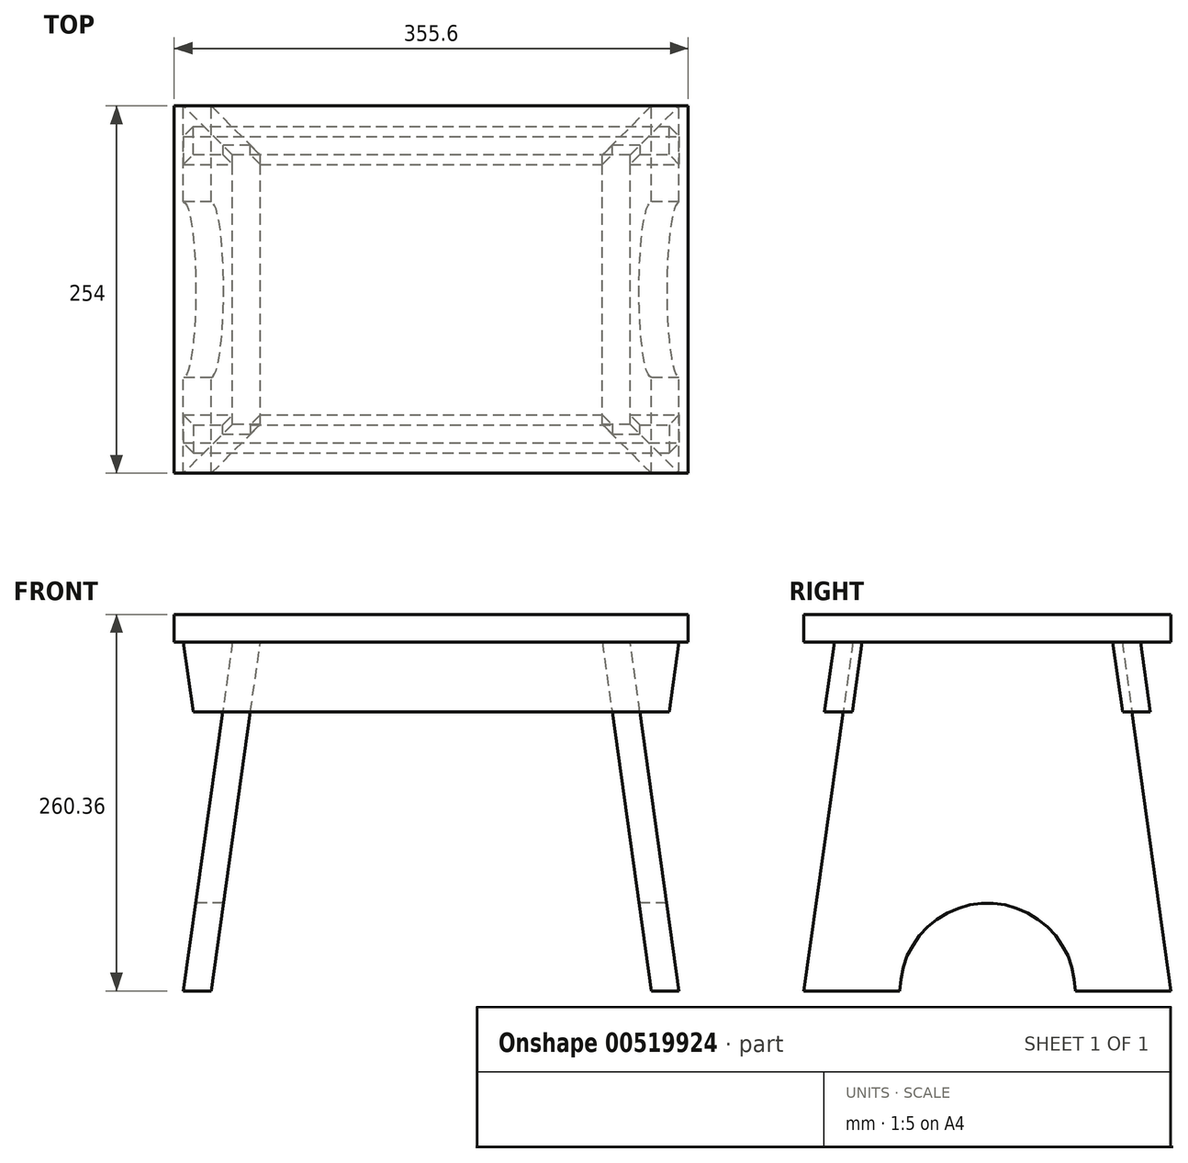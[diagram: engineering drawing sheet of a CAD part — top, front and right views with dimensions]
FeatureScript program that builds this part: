
annotation { "Feature Type Name" : "Feature", "Feature Type Description" : "" }
export const myFeature = defineFeature(function(context is Context, id is Id, definition is map)
    precondition{}
    {
        {
            var Q0;
            Q0=qCreatedBy(makeId("Front.planeOp"),FACE);
            var sketch = newSketch(context, id + "F0", { "sketchPlane" : qUnion([Q0])});
            skLineSegment(sketch, "E0.bottom", {"start": v(177.8, -9.52) * mm, "end": v(-177.8, -9.52) * mm});
            skLineSegment(sketch, "E0.top", {"start": v(177.8, 9.53) * mm, "end": v(-177.8, 9.53) * mm});
            skLineSegment(sketch, "E0.left", {"start": v(177.8, -9.52) * mm, "end": v(177.8, 9.53) * mm});
            skLineSegment(sketch, "E0.right", {"start": v(-177.8, -9.53) * mm, "end": v(-177.8, 9.52) * mm});
            skPoint(sketch, "E0.middle", {"position": v(0, 0) * mm});
            skLineSegment(sketch, "E1.bottom", {"start": v(-177.8, -9.52) * mm, "end": v(177.8, -9.52) * mm, "construction": true});
            skLineSegment(sketch, "E1.top", {"start": v(-177.8, -250.83) * mm, "end": v(177.8, -250.83) * mm, "construction": true});
            skLineSegment(sketch, "E1.left", {"start": v(-177.8, -9.53) * mm, "end": v(-177.8, -250.83) * mm, "construction": true});
            skLineSegment(sketch, "E1.right", {"start": v(177.8, -9.53) * mm, "end": v(177.8, -250.83) * mm, "construction": true});
            skLineSegment(sketch, "E2", {"start": v(0, 0) * mm, "end": v(0, 0) * mm});
            skPoint(sketch, "E2.endSnap0", {"position": v(0, -9.53) * mm});
            skLineSegment(sketch, "E3", {"start": v(-137.54, -9.53) * mm, "end": v(-171.45, -250.83) * mm});
            skLineSegment(sketch, "E4", {"start": v(-171.45, -250.83) * mm, "end": v(-152.21, -250.83) * mm});
            skLineSegment(sketch, "E5", {"start": v(-152.21, -250.83) * mm, "end": v(-118.3, -9.53) * mm});
            skLineSegment(sketch, "E6.MirrorCS", {"start": v(152.21, -250.83) * mm, "end": v(118.3, -9.52) * mm});
            skLineSegment(sketch, "E7.MirrorCS", {"start": v(137.54, -9.52) * mm, "end": v(171.45, -250.83) * mm});
            skLineSegment(sketch, "E8", {"start": v(152.21, -250.83) * mm, "end": v(171.45, -250.83) * mm});
            skLineSegment(sketch, "E9.bottom", {"start": v(-177.8, -9.52) * mm, "end": v(177.8, -9.52) * mm});
            skLineSegment(sketch, "E9.top", {"start": v(-177.8, -73.03) * mm, "end": v(177.8, -73.03) * mm});
            skLineSegment(sketch, "E9.left", {"start": v(-177.8, -9.53) * mm, "end": v(-177.8, -73.03) * mm});
            skLineSegment(sketch, "E9.right", {"start": v(177.8, -9.53) * mm, "end": v(177.8, -73.03) * mm});
            skLineSegment(sketch, "E10", {"start": v(171.45, -9.53) * mm, "end": v(162.53, -73.03) * mm});
            skLineSegment(sketch, "E11.MirrorCS", {"start": v(-171.45, -9.53) * mm, "end": v(-162.53, -73.03) * mm});
            skSolve(sketch);
        }
        {
            var Q0;
            Q0=makeQuery(id+"F0.imprint","IMPRINT",FACE,{"disambiguationData":[TD([[makeQuery(id+"F0.imprint","IMPRINT",EDGE,{"derivedFrom":sQuery(id+"F0.wireOp",EDGE,"E0.top")}),1.0]])]});
            extrude(context, id + "F1", {"entities" : qUnion([Q0]), "endBound" : BoundingType.SYMMETRIC, "depth" : 254 * mm, "offsetDistance" : 25.4 * mm});
        }
        {
            var Q0;
            {var subQ0=sQuery(id+"F0.wireOp",EDGE,"E9.bottom");var subQ1=sQuery(id+"F0.wireOp",EDGE,"E3");var subQ2=makeQuery(id+"F0.imprint","INTERSECT",VERTEX,{"derivedFrom":[subQ1,subQ0]});Q0=makeQuery(id+"F0.imprint","IMPRINT",FACE,{"disambiguationData":[TD([[makeQuery(id+"F0.imprint","IMPRINT",EDGE,{"disambiguationData":[TD([[subQ2,-1.0]])],"derivedFrom":subQ1}),1.0]])]});}
            var Q1;
            {var subQ0=sQuery(id+"F0.wireOp",EDGE,"E4");Q1=makeQuery(id+"F0.imprint","IMPRINT",FACE,{"disambiguationData":[TD([[makeQuery(id+"F0.imprint","IMPRINT",EDGE,{"derivedFrom":subQ0}),1.0]])]});}
            var Q2;
            {var subQ0=sQuery(id+"F0.wireOp",EDGE,"E8");Q2=makeQuery(id+"F0.imprint","IMPRINT",FACE,{"disambiguationData":[TD([[makeQuery(id+"F0.imprint","IMPRINT",EDGE,{"derivedFrom":subQ0}),1.0]])]});}
            var Q3;
            {var subQ0=sQuery(id+"F0.wireOp",EDGE,"E9.bottom");var subQ1=sQuery(id+"F0.wireOp",EDGE,"E6.MirrorCS");var subQ2=makeQuery(id+"F0.imprint","INTERSECT",VERTEX,{"derivedFrom":[subQ1,subQ0]});Q3=makeQuery(id+"F0.imprint","IMPRINT",FACE,{"disambiguationData":[TD([[makeQuery(id+"F0.imprint","IMPRINT",EDGE,{"disambiguationData":[TD([[subQ2,1.0]])],"derivedFrom":subQ1}),-1.0]])]});}
            var Q4;
            Q4=makeQuery(id+"F1.opExtrude","CAP_VERTEX",VERTEX,{"disambiguationData":[OSD([sQuery(id+"F0.wireOp",EDGE,"E0.left"),sQuery(id+"F0.wireOp",EDGE,"E9.bottom"),sQuery(id+"F0.wireOp",EDGE,"E9.right")])],"isStart":false});
            var Q5;
            Q5=makeQuery(id+"F1.opExtrude","CAP_VERTEX",VERTEX,{"disambiguationData":[OSD([sQuery(id+"F0.wireOp",EDGE,"E0.left"),sQuery(id+"F0.wireOp",EDGE,"E9.bottom"),sQuery(id+"F0.wireOp",EDGE,"E9.right")])],"isStart":true});
            extrude(context, id + "F2", {"entities" : qUnion([Q0, Q1, Q2, Q3]), "endBound" : BoundingType.UP_TO_VERTEX, "depth" : 25.4 * mm, "endBoundEntityVertex" : qUnion([Q4]), "offsetDistance" : 25.4 * mm, "hasSecondDirection" : true, "secondDirectionBound" : SecondDirectionBoundingType.UP_TO_VERTEX, "secondDirectionOppositeDirection" : true, "secondDirectionDepth" : 25.4 * mm, "secondDirectionBoundEntityVertex" : qUnion([Q5])});
        }
        {
            var Q0;
            Q0=qCreatedBy(makeId("Right.planeOp"),FACE);
            var sketch = newSketch(context, id + "F3", { "sketchPlane" : qUnion([Q0])});
            skLineSegment(sketch, "E12.0.0", {"start": v(127, -9.52) * mm, "end": v(-127, -9.52) * mm});
            skLineSegment(sketch, "E12.0.1", {"start": v(-127, -9.53) * mm, "end": v(-127, -250.83) * mm});
            skLineSegment(sketch, "E12.0.2", {"start": v(-127, -250.83) * mm, "end": v(127, -250.83) * mm});
            skLineSegment(sketch, "E12.0.3", {"start": v(127, -250.83) * mm, "end": v(127, -9.53) * mm});
            skLineSegment(sketch, "E13", {"start": v(-127, -250.83) * mm, "end": v(-93.09, -9.52) * mm});
            skLineSegment(sketch, "E14.MirrorCS", {"start": v(127, -250.83) * mm, "end": v(93.09, -9.52) * mm});
            skArc(sketch, "E15", {"start": v(60.85, -250.83) * mm, "mid": v(0, -189.97) * mm, "end": v(-60.85, -250.83) * mm});
            skSolve(sketch);
        }
        {
            var Q0;
            {var subQ0=sQuery(id+"F3.wireOp",EDGE,"E12.0.3");Q0=makeQuery(id+"F3.imprint","IMPRINT",FACE,{"disambiguationData":[TD([[makeQuery(id+"F3.imprint","IMPRINT",EDGE,{"derivedFrom":subQ0}),1.0]])]});}
            var Q1;
            {var subQ0=sQuery(id+"F3.wireOp",EDGE,"E15");Q1=makeQuery(id+"F3.imprint","IMPRINT",FACE,{"disambiguationData":[TD([[makeQuery(id+"F3.imprint","IMPRINT",EDGE,{"derivedFrom":subQ0}),1.0]])]});}
            var Q2;
            {var subQ0=sQuery(id+"F3.wireOp",EDGE,"E12.0.1");Q2=makeQuery(id+"F3.imprint","IMPRINT",FACE,{"disambiguationData":[TD([[makeQuery(id+"F3.imprint","IMPRINT",EDGE,{"derivedFrom":subQ0}),1.0]])]});}
            extrude(context, id + "F4", {"entities" : qUnion([Q0, Q1, Q2]), "operationType" : NewBodyOperationType.REMOVE, "endBound" : BoundingType.THROUGH_ALL, "depth" : 25.4 * mm, "offsetDistance" : 25.4 * mm, "hasSecondDirection" : true, "secondDirectionBound" : SecondDirectionBoundingType.THROUGH_ALL, "secondDirectionOppositeDirection" : true, "secondDirectionDepth" : 25.4 * mm});
        }
        {
            var Q0;
            Q0=qCreatedBy(makeId("Right.planeOp"),FACE);
            var sketch = newSketch(context, id + "F5", { "sketchPlane" : qUnion([Q0])});
            skLineSegment(sketch, "E16.0", {"start": v(-127, -250.83) * mm, "end": v(-93.09, -9.52) * mm, "construction": true});
            skLineSegment(sketch, "E17.0", {"start": v(127, -250.83) * mm, "end": v(93.09, -9.52) * mm, "construction": true});
            skLineSegment(sketch, "E18.0", {"start": v(127, -9.52) * mm, "end": v(-127, -9.52) * mm});
            skLineSegment(sketch, "E19", {"start": v(0, 13.32) * mm, "end": v(0, -82.77) * mm, "construction": true});
            skLineSegment(sketch, "E20", {"start": v(-86.68, -9.52) * mm, "end": v(-93.48, -57.95) * mm});
            skLineSegment(sketch, "E21", {"start": v(-93.48, -57.95) * mm, "end": v(-112.72, -57.95) * mm});
            skLineSegment(sketch, "E22", {"start": v(-112.72, -57.95) * mm, "end": v(-105.91, -9.52) * mm});
            skLineSegment(sketch, "E23", {"start": v(-93.48, -57.95) * mm, "end": v(10.26, -57.95) * mm, "construction": true});
            skLineSegment(sketch, "E24.MirrorCS", {"start": v(93.48, -57.95) * mm, "end": v(112.72, -57.95) * mm});
            skLineSegment(sketch, "E25.MirrorCS", {"start": v(86.68, -9.52) * mm, "end": v(93.48, -57.95) * mm});
            skLineSegment(sketch, "E26.MirrorCS", {"start": v(112.72, -57.95) * mm, "end": v(105.91, -9.52) * mm});
            skLineSegment(sketch, "E27", {"start": v(-105.91, -9.53) * mm, "end": v(-86.68, -9.53) * mm});
            skLineSegment(sketch, "E28", {"start": v(86.68, -9.52) * mm, "end": v(105.91, -9.52) * mm});
            skSolve(sketch);
        }
        {
            var Q0;
            Q0=makeQuery(id+"F5.imprint","IMPRINT",FACE,{"disambiguationData":[TD([[makeQuery(id+"F5.imprint","IMPRINT",EDGE,{"derivedFrom":sQuery(id+"F5.wireOp",EDGE,"E20")}),-1.0]])]});
            var Q1;
            Q1=makeQuery(id+"F5.imprint","IMPRINT",FACE,{"disambiguationData":[TD([[makeQuery(id+"F5.imprint","IMPRINT",EDGE,{"derivedFrom":sQuery(id+"F5.wireOp",EDGE,"E24.MirrorCS")}),1.0]])]});
            var Q2;
            Q2=makeQuery(id+"F1.opExtrude","SWEPT_FACE",FACE,{"disambiguationData":[OSD([sQuery(id+"F0.wireOp",EDGE,"E0.right")])]});
            var Q3;
            Q3=makeQuery(id+"F1.opExtrude","SWEPT_FACE",FACE,{"disambiguationData":[OSD([sQuery(id+"F0.wireOp",EDGE,"E0.left")])]});
            extrude(context, id + "F6", {"entities" : qUnion([Q0, Q1]), "endBound" : BoundingType.UP_TO_SURFACE, "oppositeDirection" : true, "depth" : 25.4 * mm, "endBoundEntityFace" : qUnion([Q2]), "offsetDistance" : 25.4 * mm, "hasSecondDirection" : true, "secondDirectionBound" : SecondDirectionBoundingType.UP_TO_SURFACE, "secondDirectionOppositeDirection" : false, "secondDirectionDepth" : 25.4 * mm, "secondDirectionBoundEntityFace" : qUnion([Q3])});
        }
        {
            var Q0;
            {var subQ0=sQuery(id+"F0.wireOp",EDGE,"E9.left");Q0=makeQuery(id+"F0.imprint","IMPRINT",FACE,{"disambiguationData":[TD([[makeQuery(id+"F0.imprint","IMPRINT",EDGE,{"derivedFrom":subQ0}),1.0]])]});}
            var Q1;
            {var subQ0=sQuery(id+"F0.wireOp",EDGE,"E9.right");Q1=makeQuery(id+"F0.imprint","IMPRINT",FACE,{"disambiguationData":[TD([[makeQuery(id+"F0.imprint","IMPRINT",EDGE,{"derivedFrom":subQ0}),-1.0]])]});}
            extrude(context, id + "F7", {"entities" : qUnion([Q0, Q1]), "operationType" : NewBodyOperationType.REMOVE, "endBound" : BoundingType.THROUGH_ALL, "oppositeDirection" : true, "depth" : 25.4 * mm, "offsetDistance" : 25.4 * mm, "hasSecondDirection" : true, "secondDirectionBound" : SecondDirectionBoundingType.THROUGH_ALL, "secondDirectionOppositeDirection" : false, "secondDirectionDepth" : 25.4 * mm});
        }
        {
            var Q0;
            Q0=makeQuery(id+"F2.opExtrude","SWEPT_BODY",BODY,{"disambiguationData":[OSD([sQuery(id+"F0.wireOp",EDGE,"E3"),sQuery(id+"F0.wireOp",EDGE,"E4"),sQuery(id+"F0.wireOp",EDGE,"E5"),sQuery(id+"F0.wireOp",EDGE,"E9.bottom")])]});
            var Q1;
            Q1=makeQuery(id+"F6.opExtrude","SWEPT_BODY",BODY,{"disambiguationData":[OSD([sQuery(id+"F5.wireOp",EDGE,"E24.MirrorCS"),sQuery(id+"F5.wireOp",EDGE,"E25.MirrorCS"),sQuery(id+"F5.wireOp",EDGE,"E26.MirrorCS"),sQuery(id+"F5.wireOp",EDGE,"E28")])]});
            var Q2;
            Q2=makeQuery(id+"F6.opExtrude","SWEPT_BODY",BODY,{"disambiguationData":[OSD([sQuery(id+"F5.wireOp",EDGE,"E20"),sQuery(id+"F5.wireOp",EDGE,"E21"),sQuery(id+"F5.wireOp",EDGE,"E22"),sQuery(id+"F5.wireOp",EDGE,"E27")])]});
            booleanBodies(context, id + "F8", {"operationType" : BooleanOperationType.SUBTRACTION, "tools" : qUnion([Q0]), "targets" : qUnion([Q1, Q2]), "keepTools" : true});
        }
        {
            var Q0;
            Q0=makeQuery(id+"F2.opExtrude","SWEPT_BODY",BODY,{"disambiguationData":[OSD([sQuery(id+"F0.wireOp",EDGE,"E6.MirrorCS"),sQuery(id+"F0.wireOp",EDGE,"E7.MirrorCS"),sQuery(id+"F0.wireOp",EDGE,"E8"),sQuery(id+"F0.wireOp",EDGE,"E9.bottom")])]});
            var Q1;
            Q1=makeQuery(id+"F6.opExtrude","SWEPT_BODY",BODY,{"disambiguationData":[OSD([sQuery(id+"F5.wireOp",EDGE,"E20"),sQuery(id+"F5.wireOp",EDGE,"E21"),sQuery(id+"F5.wireOp",EDGE,"E22"),sQuery(id+"F5.wireOp",EDGE,"E27")])]});
            var Q2;
            Q2=makeQuery(id+"F6.opExtrude","SWEPT_BODY",BODY,{"disambiguationData":[OSD([sQuery(id+"F5.wireOp",EDGE,"E24.MirrorCS"),sQuery(id+"F5.wireOp",EDGE,"E25.MirrorCS"),sQuery(id+"F5.wireOp",EDGE,"E26.MirrorCS"),sQuery(id+"F5.wireOp",EDGE,"E28")])]});
            booleanBodies(context, id + "F9", {"operationType" : BooleanOperationType.SUBTRACTION, "tools" : qUnion([Q0]), "targets" : qUnion([Q1, Q2]), "keepTools" : true});
        }
    });
